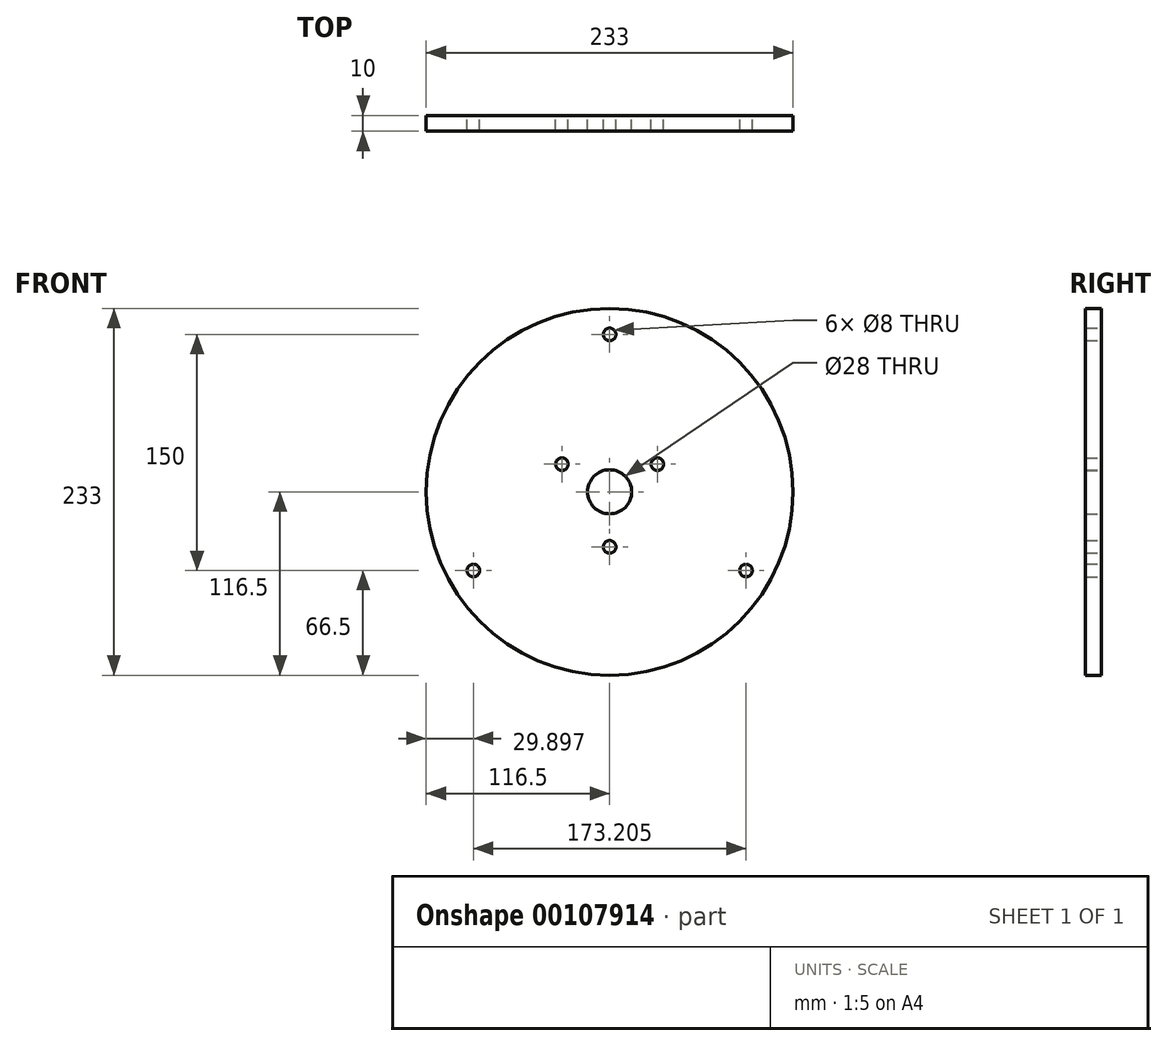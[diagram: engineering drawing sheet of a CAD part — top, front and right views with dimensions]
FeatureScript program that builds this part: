
annotation { "Feature Type Name" : "Feature", "Feature Type Description" : "" }
export const myFeature = defineFeature(function(context is Context, id is Id, definition is map)
    precondition{}
    {
        {
            var Q0;
            Q0=qCreatedBy(makeId("Front.planeOp"),FACE);
            var sketch = newSketch(context, id + "F0", { "sketchPlane" : qUnion([Q0])});
            skCircle(sketch, "E0", {"center": v(0, 0) * mm, "radius": 116.5 * mm});
            skCircle(sketch, "E1", {"center": v(0, 0) * mm, "radius": 14 * mm});
            skCircle(sketch, "E2", {"center": v(0, -35) * mm, "radius": 4 * mm});
            skCircle(sketch, "E3", {"center": v(0, 100) * mm, "radius": 4 * mm});
            skCircle(sketch, "E4.1.0", {"center": v(-86.6, -50) * mm, "radius": 4 * mm});
            skCircle(sketch, "E4.2.0", {"center": v(86.6, -50) * mm, "radius": 4 * mm});
            skCircle(sketch, "E5.1.0", {"center": v(30.31, 17.5) * mm, "radius": 4 * mm});
            skCircle(sketch, "E5.2.0", {"center": v(-30.31, 17.5) * mm, "radius": 4 * mm});
            skCircle(sketch, "E6", {"center": v(0, 0) * mm, "radius": 150 * mm, "construction": true});
            skSolve(sketch);
        }
        {
            var Q0;
            Q0=makeQuery(id+"F0.imprint","IMPRINT",FACE,{"disambiguationData":[TD([[makeQuery(id+"F0.imprint","IMPRINT",EDGE,{"derivedFrom":sQuery(id+"F0.wireOp",EDGE,"E0")}),1.0]])]});
            extrude(context, id + "F1", {"entities" : qUnion([Q0]), "depth" : 10 * mm, "offsetDistance" : 25 * mm});
        }
    });
